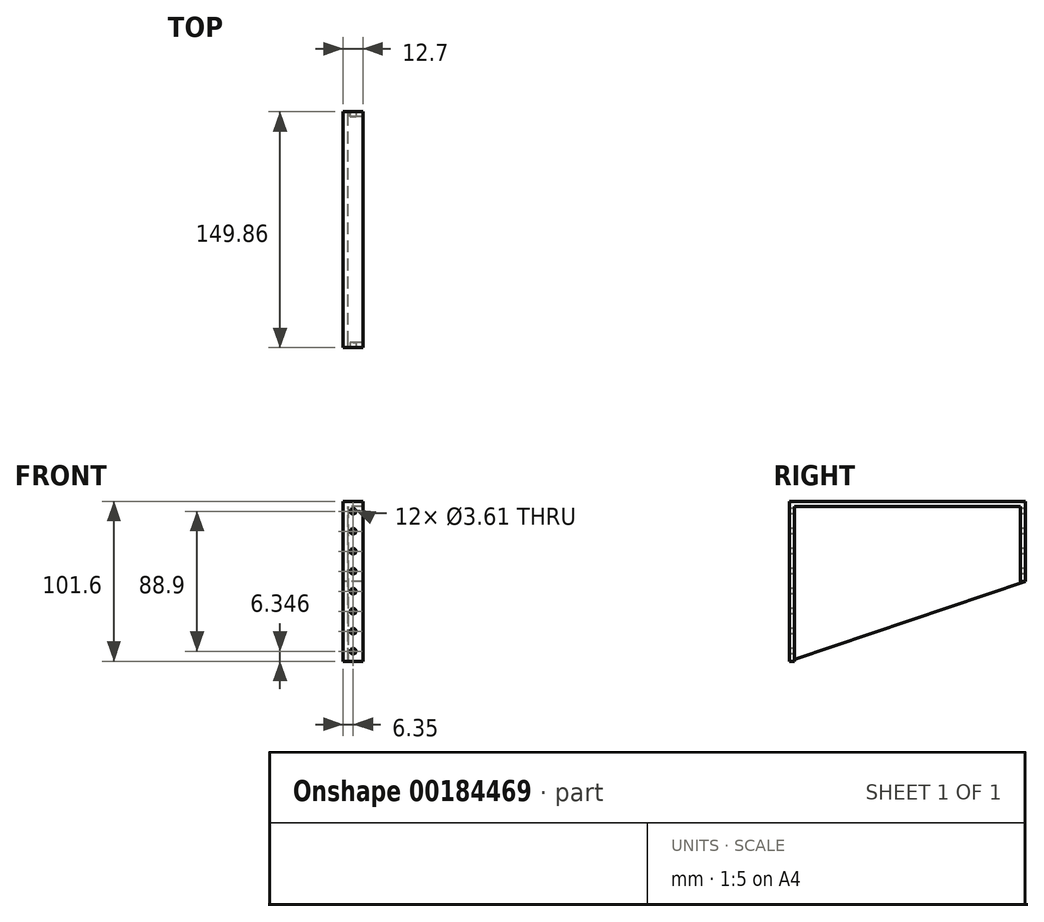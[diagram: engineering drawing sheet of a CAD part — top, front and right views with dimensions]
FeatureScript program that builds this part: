
annotation { "Feature Type Name" : "Feature", "Feature Type Description" : "" }
export const myFeature = defineFeature(function(context is Context, id is Id, definition is map)
    precondition{}
    {
        {
            var Q0;
            Q0=qCreatedBy(makeId("Right.planeOp"),FACE);
            var sketch = newSketch(context, id + "F0", { "sketchPlane" : qUnion([Q0])});
            skLineSegment(sketch, "E0", {"start": v(-48.32, -41.32) * mm, "end": v(-48.32, 60.28) * mm});
            skLineSegment(sketch, "E1", {"start": v(-48.32, 60.28) * mm, "end": v(101.54, 60.28) * mm});
            skLineSegment(sketch, "E2", {"start": v(-48.32, -41.32) * mm, "end": v(101.54, 9.48) * mm});
            skLineSegment(sketch, "E3", {"start": v(101.54, 9.48) * mm, "end": v(101.54, 60.28) * mm});
            skSolve(sketch);
        }
        {
            var Q0;
            Q0=makeQuery(id+"F0.imprint","IMPRINT",FACE,{"disambiguationData":[TD([[makeQuery(id+"F0.imprint","IMPRINT",EDGE,{"derivedFrom":sQuery(id+"F0.wireOp",EDGE,"E0")}),-1.0]])]});
            extrude(context, id + "F1", {"entities" : qUnion([Q0]), "depth" : 3.17 * mm});
        }
        {
            var Q0;
            Q0=makeQuery(id+"F1.opExtrude","CAP_FACE",FACE,{"disambiguationData":[OSD([sQuery(id+"F0.wireOp",EDGE,"E0"),sQuery(id+"F0.wireOp",EDGE,"E1"),sQuery(id+"F0.wireOp",EDGE,"h6iIoQ3C-x4Wb-YAmo-Urja-DkJstJPnqKBA")])],"isStart":false});
            var sketch = newSketch(context, id + "F2", { "sketchPlane" : qUnion([Q0])});
            skLineSegment(sketch, "E4.top", {"start": v(-48.32, -41.32) * mm, "end": v(-45.15, -41.32) * mm});
            skLineSegment(sketch, "E4.left", {"start": v(-48.32, 60.28) * mm, "end": v(-48.32, -41.32) * mm});
            skLineSegment(sketch, "E5", {"start": v(-48.32, 60.28) * mm, "end": v(-48.32, 60.28) * mm});
            skLineSegment(sketch, "E6", {"start": v(-48.32, 60.28) * mm, "end": v(-48.32, 57.1) * mm});
            skLineSegment(sketch, "E7", {"start": v(-45.15, 57.1) * mm, "end": v(-45.15, -41.32) * mm});
            skLineSegment(sketch, "E8", {"start": v(101.54, 57.1) * mm, "end": v(101.54, 60.28) * mm});
            skLineSegment(sketch, "E9", {"start": v(101.54, 60.28) * mm, "end": v(-48.32, 60.28) * mm});
            skLineSegment(sketch, "E10", {"start": v(101.54, 57.1) * mm, "end": v(101.54, 9.48) * mm});
            skLineSegment(sketch, "E11", {"start": v(101.54, 9.48) * mm, "end": v(98.36, 9.48) * mm});
            skLineSegment(sketch, "E12", {"start": v(98.36, 9.48) * mm, "end": v(98.36, 57.1) * mm});
            skLineSegment(sketch, "E13", {"start": v(-45.15, 57.1) * mm, "end": v(98.36, 57.1) * mm});
            skSolve(sketch);
        }
        {
            var Q0;
            Q0 = qSketchRegion(id + "F2", true);
            extrude(context, id + "F3", {"entities" : qUnion([Q0]), "operationType" : NewBodyOperationType.ADD, "depth" : 9.52 * mm});
        }
        {
            var Q0;
            Q0=makeQuery(id+"F3.boolean.opBoolean","MERGE",FACE,{"derivedFrom":[makeQuery(id+"F1.opExtrude","SWEPT_FACE",FACE,{"disambiguationData":[OSD([sQuery(id+"F0.wireOp",EDGE,"E0")])]}),makeQuery(id+"F3.opExtrude","SWEPT_FACE",FACE,{"disambiguationData":[OSD([sQuery(id+"F2.wireOp",EDGE,"E4.left"),sQuery(id+"F2.wireOp",EDGE,"E6")])]})]});
            var sketch = newSketch(context, id + "F4", { "sketchPlane" : qUnion([Q0])});
            skCircle(sketch, "E14", {"center": v(6.35, -34.97) * mm, "radius": 1.8 * mm});
            skCircle(sketch, "E15.0.1.0", {"center": v(6.35, -22.27) * mm, "radius": 1.8 * mm});
            skCircle(sketch, "E15.0.2.0", {"center": v(6.35, -9.57) * mm, "radius": 1.8 * mm});
            skCircle(sketch, "E15.0.3.0", {"center": v(6.35, 3.13) * mm, "radius": 1.8 * mm});
            skCircle(sketch, "E15.0.4.0", {"center": v(6.35, 15.83) * mm, "radius": 1.8 * mm});
            skCircle(sketch, "E15.0.5.0", {"center": v(6.35, 28.53) * mm, "radius": 1.8 * mm});
            skCircle(sketch, "E15.0.6.0", {"center": v(6.35, 41.23) * mm, "radius": 1.8 * mm});
            skCircle(sketch, "E15.0.7.0", {"center": v(6.35, 53.93) * mm, "radius": 1.8 * mm});
            skLineSegment(sketch, "E15.direction2", {"start": v(6.35, -34.97) * mm, "end": v(6.35, -22.27) * mm, "construction": true});
            skSolve(sketch);
        }
        {
            var Q0;
            Q0 = qSketchRegion(id + "F4", true);
            extrude(context, id + "F5", {"entities" : qUnion([Q0]), "operationType" : NewBodyOperationType.REMOVE, "endBound" : BoundingType.THROUGH_ALL, "oppositeDirection" : true, "depth" : 25.4 * mm});
        }
    });
